# Revit family: 3-107-xx Solis Fan
name_source: partatom
category: Generic Models
units: mm (PartAtom-declared; Revit-internal decimal feet)

## family parameters
Always vertical = Yes
Can host rebar = No
Cut with Voids When Loaded = No
Host = Ceiling
Part Type = Normal
Room Calculation Point = No
Round Connector Dimension = Use Diameter
Shared = No

## types (3) — shared parameters
Main Diffuser = Matte White Acrylic
Manufacturer = Oxygen - Lighting & Fans
Model = 3-107-xx /37-107-xx Solis Fan
References = Ref. 3 = 120 V / Ref. 37 = 277 V
URL = www.oxygenlighting.com
Voltage = 120 V
Voltage Input = 120 V or 277 V - 50/60 Hz

## per-type parameters (varying)
| type | Blade Finish | Metal Finish |
| 3-107-15 / Black - Black Blades | 15 - Black | 15 - Black |
| 3-107-24 / Satin Nickel - Satin Nicke Blades | 24 - Satin Nickel | 24 - Satin Nickel |
| 3-107-6 / White - White Blades | 6 - White | 6 - White |

## geometry (parser evidence)
native form markers: Blend x5, Extrusion x1, Sweep x11
no freeform markers — native parametric forms only
